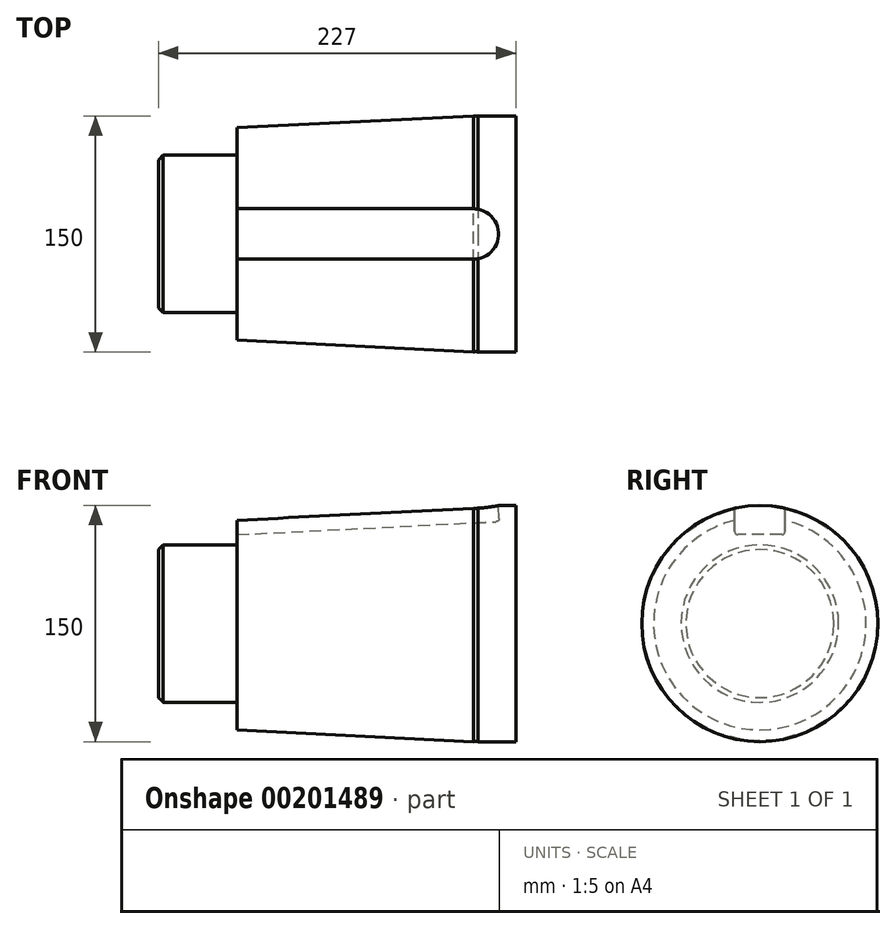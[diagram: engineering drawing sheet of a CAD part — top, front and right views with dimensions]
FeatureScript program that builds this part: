
annotation { "Feature Type Name" : "Feature", "Feature Type Description" : "" }
export const myFeature = defineFeature(function(context is Context, id is Id, definition is map)
    precondition{}
    {
        {
            var Q0;
            Q0=qCreatedBy(makeId("Front.planeOp"),FACE);
            var sketch = newSketch(context, id + "F0", { "sketchPlane" : qUnion([Q0])});
            skLineSegment(sketch, "E0", {"start": v(0, 0) * mm, "end": v(0, 50) * mm});
            skLineSegment(sketch, "E1", {"start": v(0, 50) * mm, "end": v(50, 50) * mm});
            skLineSegment(sketch, "E2", {"start": v(50, 50) * mm, "end": v(50, 67.5) * mm});
            skLineSegment(sketch, "E3", {"start": v(50, 67.5) * mm, "end": v(200, 75) * mm});
            skLineSegment(sketch, "E4", {"start": v(200, 75) * mm, "end": v(227, 75) * mm});
            skLineSegment(sketch, "E5", {"start": v(227, 75) * mm, "end": v(227, 0) * mm});
            skLineSegment(sketch, "E6", {"start": v(227, 0) * mm, "end": v(0, 0) * mm});
            skSolve(sketch);
        }
        {
            var Q0;
            Q0 = qSketchRegion(id + "F0", true);
            var Q1;
            Q1=sQuery(id+"F0.wireOp",EDGE,"E6");
            revolve(context, id + "F1", {"entities" : qUnion([Q0]), "axis" : qUnion([Q1]), "revolveType" : RevolveType.FULL});
        }
        {
            var Q0;
            Q0=sQuery(id+"F0.wireOp",EDGE,"E3");
            cPlane(context, id + "F2", {"entities" : qUnion([Q0]), "cplaneType" : CPlaneType.LINE_ANGLE, "offset" : 25 * mm, "angle" : 90 * degree, "width" : 150 * mm, "height" : 150 * mm});
        }
        {
            var Q0;
            Q0=qCreatedBy(id+"F2.planeOp",FACE);
            var sketch = newSketch(context, id + "F3", { "sketchPlane" : qUnion([Q0])});
            skLineSegment(sketch, "E7.bottom", {"start": v(0, -16) * mm, "end": v(203.5, -16) * mm});
            skLineSegment(sketch, "E7.top", {"start": v(0, 16) * mm, "end": v(203.5, 16) * mm});
            skLineSegment(sketch, "E7.left", {"start": v(0, -16) * mm, "end": v(0, 16) * mm});
            skLineSegment(sketch, "E7.right", {"start": v(203.5, -16) * mm, "end": v(203.5, 16) * mm, "construction": true});
            skArc(sketch, "E8", {"start": v(203.5, 16) * mm, "mid": v(219.5, 0) * mm, "end": v(203.5, -16) * mm});
            skSolve(sketch);
        }
        {
            var Q0;
            Q0=makeQuery(id+"F3.imprint","IMPRINT",FACE,{"disambiguationData":[TD([[makeQuery(id+"F3.imprint","IMPRINT",EDGE,{"derivedFrom":sQuery(id+"F3.wireOp",EDGE,"E7.bottom")}),1.0]])]});
            extrude(context, id + "F4", {"entities" : qUnion([Q0]), "operationType" : NewBodyOperationType.REMOVE, "oppositeDirection" : true, "depth" : 11 * mm});
        }
        {
            var Q0;
            Q0=qCreatedBy(makeId("Front.planeOp"),FACE);
            var sketch = newSketch(context, id + "F5", { "sketchPlane" : qUnion([Q0])});
            skCircle(sketch, "E9", {"center": v(201.5, 79.8) * mm, "radius": 5 * mm});
            skSolve(sketch);
        }
        {
            var Q0;
            Q0=makeQuery(id+"F5.imprint","IMPRINT",FACE,{"disambiguationData":[TD([[makeQuery(id+"F5.imprint","IMPRINT",EDGE,{"derivedFrom":sQuery(id+"F5.wireOp",EDGE,"E9")}),1.0]])]});
            var Q1;
            Q1=sQuery(id+"F0.wireOp",EDGE,"E6");
            revolve(context, id + "F6", {"operationType" : NewBodyOperationType.REMOVE, "entities" : qUnion([Q0]), "axis" : qUnion([Q1]), "revolveType" : RevolveType.FULL, "oppositeDirection" : true});
        }
        {
            var Q0;
            Q0=makeQuery(id+"F1.opRevolve","SWEPT_EDGE",EDGE,{"disambiguationData":[OSD([sQuery(id+"F0.wireOp",EDGE,"E0"),sQuery(id+"F0.wireOp",EDGE,"E1")])]});
            chamfer(context, id + "F7", {"entities" : qUnion([Q0]), "width" : 3 * mm, "tangentPropagation" : true});
        }
        {
            var Q0;
            Q0=makeQuery(id+"F4.boolean.opBoolean","COPY",EDGE,{"derivedFrom":makeQuery(id+"F4.opExtrude","CAP_EDGE",EDGE,{"disambiguationData":[OSD([sQuery(id+"F3.wireOp",EDGE,"E7.top")])],"isStart":false})});
            var Q1;
            Q1=makeQuery(id+"F2VtAiYCbyme89R_1.1.F4.boolean.opBoolean","COPY",EDGE,{"derivedFrom":makeQuery(id+"F2VtAiYCbyme89R_1.1.F4.opExtrude","CAP_EDGE",EDGE,{"disambiguationData":[OSD([sQuery(id+"F3.wireOp",EDGE,"E7.top")])],"isStart":false})});
            fillet(context, id + "F8", {"entities" : qUnion([Q0, Q1]), "radius" : 2 * mm, "tangentPropagation" : true, "allowEdgeOverflow" : false});
        }
    });
